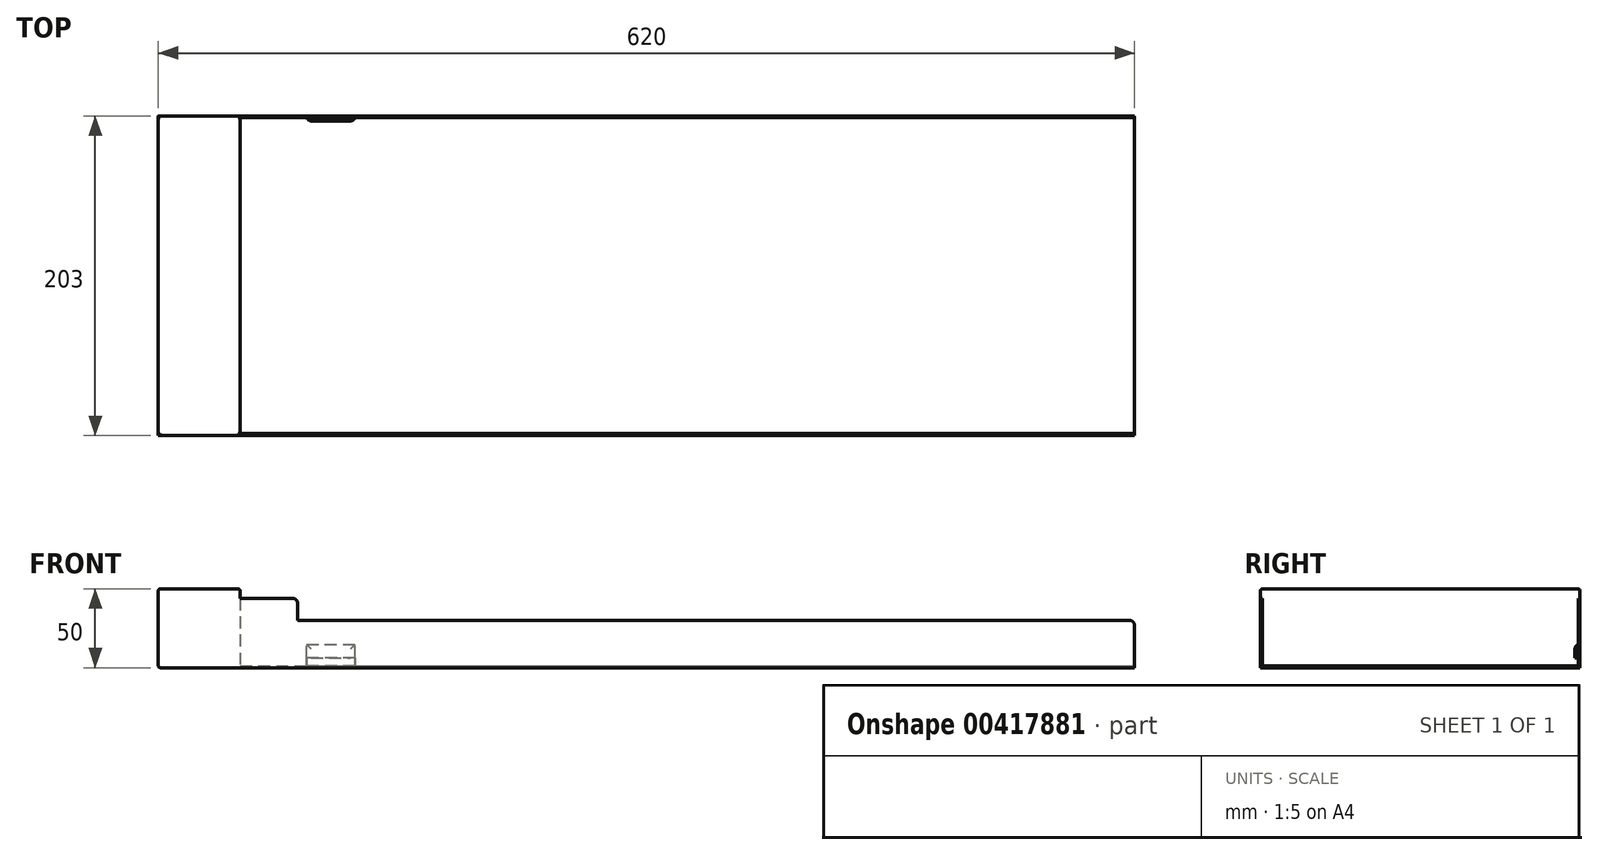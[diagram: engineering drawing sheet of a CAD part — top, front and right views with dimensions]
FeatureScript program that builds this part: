
annotation { "Feature Type Name" : "Feature", "Feature Type Description" : "" }
export const myFeature = defineFeature(function(context is Context, id is Id, definition is map)
    precondition{}
    {
        {
            var Q0;
            Q0=qCreatedBy(makeId("Top.planeOp"),FACE);
            var sketch = newSketch(context, id + "F0", { "sketchPlane" : qUnion([Q0])});
            skLineSegment(sketch, "E0.bottom", {"start": v(-97.62, 164.37) * mm, "end": v(522.38, 164.37) * mm});
            skLineSegment(sketch, "E0.top", {"start": v(-97.62, -38.63) * mm, "end": v(522.38, -38.63) * mm});
            skLineSegment(sketch, "E0.left", {"start": v(-97.62, 164.37) * mm, "end": v(-97.62, -38.63) * mm});
            skLineSegment(sketch, "E0.right", {"start": v(522.38, 164.37) * mm, "end": v(522.38, -38.63) * mm});
            skLineSegment(sketch, "E1.0", {"start": v(-45.62, 164.37) * mm, "end": v(-45.62, -38.63) * mm});
            skLineSegment(sketch, "E2.0", {"start": v(-97.62, 163.17) * mm, "end": v(522.38, 163.17) * mm});
            skLineSegment(sketch, "E3.0", {"start": v(-97.62, -37.43) * mm, "end": v(522.38, -37.43) * mm});
            skLineSegment(sketch, "E4", {"start": v(-9.17, -38.63) * mm, "end": v(-9.17, 164.37) * mm});
            skSolve(sketch);
        }
        {
            var Q0;
            {var subQ0=sQuery(id+"F0.wireOp",EDGE,"E0.left");Q0=makeQuery(id+"F0.imprint","IMPRINT",FACE,{"disambiguationData":[TD([[makeQuery(id+"F0.imprint","IMPRINT",EDGE,{"derivedFrom":subQ0}),1.0]])]});}
            extrude(context, id + "F1", {"entities" : qUnion([Q0]), "depth" : 50 * mm});
        }
        {
            var Q0;
            {var subQ0=sQuery(id+"F0.wireOp",EDGE,"E1.0");var subQ1=sQuery(id+"F0.wireOp",EDGE,"E0.top");var subQ2=makeQuery(id+"F0.imprint","INTERSECT",VERTEX,{"derivedFrom":[subQ1,subQ0]});Q0=makeQuery(id+"F0.imprint","IMPRINT",FACE,{"disambiguationData":[TD([[makeQuery(id+"F0.imprint","IMPRINT",EDGE,{"disambiguationData":[TD([[subQ2,-1.0]])],"derivedFrom":subQ1}),1.0]])]});}
            var Q1;
            {var subQ0=sQuery(id+"F0.wireOp",EDGE,"E1.0");var subQ1=sQuery(id+"F0.wireOp",EDGE,"E0.bottom");var subQ2=makeQuery(id+"F0.imprint","INTERSECT",VERTEX,{"derivedFrom":[subQ1,subQ0]});Q1=makeQuery(id+"F0.imprint","IMPRINT",FACE,{"disambiguationData":[TD([[makeQuery(id+"F0.imprint","IMPRINT",EDGE,{"disambiguationData":[TD([[subQ2,-1.0]])],"derivedFrom":subQ1}),-1.0]])]});}
            extrude(context, id + "F2", {"entities" : qUnion([Q0, Q1]), "operationType" : NewBodyOperationType.ADD, "depth" : 44 * mm});
        }
        {
            var Q0;
            {var subQ0=sQuery(id+"F0.wireOp",EDGE,"E0.right");var subQ1=sQuery(id+"F0.wireOp",EDGE,"E0.bottom");var subQ2=makeQuery(id+"F0.imprint","INTERSECT",VERTEX,{"derivedFrom":[subQ1,subQ0]});Q0=makeQuery(id+"F0.imprint","IMPRINT",FACE,{"disambiguationData":[TD([[makeQuery(id+"F0.imprint","IMPRINT",EDGE,{"disambiguationData":[TD([[subQ2,1.0]])],"derivedFrom":subQ1}),-1.0]])]});}
            var Q1;
            {var subQ0=sQuery(id+"F0.wireOp",EDGE,"E0.right");var subQ1=sQuery(id+"F0.wireOp",EDGE,"E0.top");var subQ2=makeQuery(id+"F0.imprint","INTERSECT",VERTEX,{"derivedFrom":[subQ1,subQ0]});Q1=makeQuery(id+"F0.imprint","IMPRINT",FACE,{"disambiguationData":[TD([[makeQuery(id+"F0.imprint","IMPRINT",EDGE,{"disambiguationData":[TD([[subQ2,1.0]])],"derivedFrom":subQ1}),1.0]])]});}
            extrude(context, id + "F3", {"entities" : qUnion([Q0, Q1]), "operationType" : NewBodyOperationType.ADD, "depth" : 30 * mm});
        }
        {
            var Q0;
            {var subQ0=sQuery(id+"F0.wireOp",EDGE,"E2.0");var subQ1=sQuery(id+"F0.wireOp",EDGE,"E0.right");var subQ2=makeQuery(id+"F0.imprint","INTERSECT",VERTEX,{"derivedFrom":[subQ1,subQ0]});Q0=makeQuery(id+"F0.imprint","IMPRINT",FACE,{"disambiguationData":[TD([[makeQuery(id+"F0.imprint","IMPRINT",EDGE,{"disambiguationData":[TD([[subQ2,-1.0]])],"derivedFrom":subQ1}),-1.0]])]});}
            var Q1;
            {var subQ0=sQuery(id+"F0.wireOp",EDGE,"E2.0");var subQ1=sQuery(id+"F0.wireOp",EDGE,"E1.0");var subQ2=makeQuery(id+"F0.imprint","INTERSECT",VERTEX,{"derivedFrom":[subQ1,subQ0]});Q1=makeQuery(id+"F0.imprint","IMPRINT",FACE,{"disambiguationData":[TD([[makeQuery(id+"F0.imprint","IMPRINT",EDGE,{"disambiguationData":[TD([[subQ2,-1.0]])],"derivedFrom":subQ1}),1.0]])]});}
            extrude(context, id + "F4", {"entities" : qUnion([Q0, Q1]), "operationType" : NewBodyOperationType.ADD, "depth" : 1.2 * mm});
        }
        {
            var Q0;
            Q0=makeQuery(id+"F1.opExtrude","CAP_EDGE",EDGE,{"disambiguationData":[OSD([sQuery(id+"F0.wireOp",EDGE,"E0.top")])],"isStart":false});
            var Q1;
            Q1=makeQuery(id+"F1.opExtrude","CAP_EDGE",EDGE,{"disambiguationData":[OSD([sQuery(id+"F0.wireOp",EDGE,"E0.bottom")])],"isStart":false});
            var Q2;
            Q2=makeQuery(id+"F1.opExtrude","CAP_EDGE",EDGE,{"disambiguationData":[OSD([sQuery(id+"F0.wireOp",EDGE,"E0.left")])],"isStart":false});
            var Q3;
            Q3=makeQuery(id+"F1.opExtrude","CAP_EDGE",EDGE,{"disambiguationData":[OSD([sQuery(id+"F0.wireOp",EDGE,"E0.left")])],"isStart":true});
            var Q4;
            Q4=makeQuery(id+"F1.opExtrude","CAP_EDGE",EDGE,{"disambiguationData":[OSD([sQuery(id+"F0.wireOp",EDGE,"E1.0")])],"isStart":false});
            var Q5;
            {var subQ0=sQuery(id+"F0.wireOp",EDGE,"E1.0");Q5=makeQuery(id+"F2.opExtrude","CAP_EDGE",EDGE,{"disambiguationData":[OSD([subQ0]),TDD([makeQuery(id+"F0.imprint","IMPRINT",EDGE,{"disambiguationData":[TD([[makeQuery(id+"F0.imprint","INTERSECT",VERTEX,{"derivedFrom":[sQuery(id+"F0.wireOp",EDGE,"E0.top"),subQ0]}),1.0]])],"derivedFrom":subQ0})])],"isStart":false});}
            fillet(context, id + "F5", {"entities" : qUnion([Q0, Q1, Q2, Q3, Q4, Q5]), "radius" : 1.2 * mm, "tangentPropagation" : true, "allowEdgeOverflow" : false});
        }
        {
            var Q0;
            {var subQ0=sQuery(id+"F0.wireOp",EDGE,"E4");Q0=makeQuery(id+"F2.opExtrude","CAP_EDGE",EDGE,{"disambiguationData":[OSD([subQ0]),TDD([makeQuery(id+"F0.imprint","IMPRINT",EDGE,{"disambiguationData":[TD([[makeQuery(id+"F0.imprint","INTERSECT",VERTEX,{"derivedFrom":[sQuery(id+"F0.wireOp",EDGE,"E0.top"),subQ0]}),-1.0]])],"derivedFrom":subQ0})])],"isStart":false});}
            var Q1;
            {var subQ0=sQuery(id+"F0.wireOp",EDGE,"E0.right");Q1=makeQuery(id+"F3.opExtrude","CAP_EDGE",EDGE,{"disambiguationData":[OSD([subQ0]),TDD([makeQuery(id+"F0.imprint","IMPRINT",EDGE,{"disambiguationData":[TD([[makeQuery(id+"F0.imprint","INTERSECT",VERTEX,{"derivedFrom":[sQuery(id+"F0.wireOp",EDGE,"E0.top"),subQ0]}),1.0]])],"derivedFrom":subQ0})])],"isStart":false});}
            var Q2;
            {var subQ0=sQuery(id+"F0.wireOp",EDGE,"E0.right");Q2=makeQuery(id+"F3.opExtrude","CAP_EDGE",EDGE,{"disambiguationData":[OSD([subQ0]),TDD([makeQuery(id+"F0.imprint","IMPRINT",EDGE,{"disambiguationData":[TD([[makeQuery(id+"F0.imprint","INTERSECT",VERTEX,{"derivedFrom":[sQuery(id+"F0.wireOp",EDGE,"E0.bottom"),subQ0]}),-1.0]])],"derivedFrom":subQ0})])],"isStart":false});}
            var Q3;
            {var subQ0=sQuery(id+"F0.wireOp",EDGE,"E4");Q3=makeQuery(id+"F2.opExtrude","CAP_EDGE",EDGE,{"disambiguationData":[OSD([subQ0]),TDD([makeQuery(id+"F0.imprint","IMPRINT",EDGE,{"disambiguationData":[TD([[makeQuery(id+"F0.imprint","INTERSECT",VERTEX,{"derivedFrom":[sQuery(id+"F0.wireOp",EDGE,"E0.bottom"),subQ0]}),1.0]])],"derivedFrom":subQ0})])],"isStart":false});}
            var Q4;
            {var subQ0=sQuery(id+"F0.wireOp",EDGE,"E4");Q4=makeQuery(id+"F3.opExtrude","CAP_EDGE",EDGE,{"disambiguationData":[OSD([subQ0]),TDD([makeQuery(id+"F0.imprint","IMPRINT",EDGE,{"disambiguationData":[TD([[makeQuery(id+"F0.imprint","INTERSECT",VERTEX,{"derivedFrom":[sQuery(id+"F0.wireOp",EDGE,"E0.bottom"),subQ0]}),1.0]])],"derivedFrom":subQ0})])],"isStart":false});}
            var Q5;
            {var subQ0=sQuery(id+"F0.wireOp",EDGE,"E4");Q5=makeQuery(id+"F3.opExtrude","CAP_EDGE",EDGE,{"disambiguationData":[OSD([subQ0]),TDD([makeQuery(id+"F0.imprint","IMPRINT",EDGE,{"disambiguationData":[TD([[makeQuery(id+"F0.imprint","INTERSECT",VERTEX,{"derivedFrom":[sQuery(id+"F0.wireOp",EDGE,"E0.top"),subQ0]}),-1.0]])],"derivedFrom":subQ0})])],"isStart":false});}
            var Q6;
            {var subQ0=sQuery(id+"F0.wireOp",EDGE,"E1.0");Q6=makeQuery(id+"F2.opExtrude","CAP_EDGE",EDGE,{"disambiguationData":[OSD([subQ0]),TDD([makeQuery(id+"F0.imprint","IMPRINT",EDGE,{"disambiguationData":[TD([[makeQuery(id+"F0.imprint","INTERSECT",VERTEX,{"derivedFrom":[sQuery(id+"F0.wireOp",EDGE,"E0.top"),subQ0]}),1.0]])],"derivedFrom":subQ0})])],"isStart":false});}
            fillet(context, id + "F6", {"entities" : qUnion([Q0, Q1, Q2, Q3, Q4, Q5, Q6]), "radius" : 3 * mm, "tangentPropagation" : true, "allowEdgeOverflow" : false});
        }
        {
            var Q0;
            {var subQ0=sQuery(id+"F0.wireOp",EDGE,"E2.0");Q0=makeQuery(id+"F3.boolean.opBoolean","MERGE",FACE,{"derivedFrom":[makeQuery(id+"F2.opExtrude","SWEPT_FACE",FACE,{"disambiguationData":[OSD([subQ0])]}),makeQuery(id+"F3.opExtrude","SWEPT_FACE",FACE,{"disambiguationData":[OSD([subQ0])]})]});}
            var sketch = newSketch(context, id + "F7", { "sketchPlane" : qUnion([Q0])});
            skLineSegment(sketch, "E5.bottom", {"start": v(-3.34, 1.18) * mm, "end": v(27.29, 1.18) * mm});
            skLineSegment(sketch, "E5.top", {"start": v(-3.34, 6.2) * mm, "end": v(27.29, 6.2) * mm});
            skLineSegment(sketch, "E5.left", {"start": v(-3.34, 1.18) * mm, "end": v(-3.34, 6.2) * mm});
            skLineSegment(sketch, "E5.right", {"start": v(27.29, 1.18) * mm, "end": v(27.29, 6.2) * mm});
            skSolve(sketch);
        }
        {
            var Q0;
            Q0 = qSketchRegion(id + "F7", true);
            extrude(context, id + "F8", {"entities" : qUnion([Q0]), "operationType" : NewBodyOperationType.REMOVE, "oppositeDirection" : true, "depth" : 25 * mm});
        }
        {
            var Q0;
            {var subQ0=sQuery(id+"F0.wireOp",EDGE,"E2.0");Q0=makeQuery(id+"F3.boolean.opBoolean","MERGE",FACE,{"derivedFrom":[makeQuery(id+"F2.opExtrude","SWEPT_FACE",FACE,{"disambiguationData":[OSD([subQ0])]}),makeQuery(id+"F3.opExtrude","SWEPT_FACE",FACE,{"disambiguationData":[OSD([subQ0])]})]});}
            var sketch = newSketch(context, id + "F9", { "sketchPlane" : qUnion([Q0])});
            skLineSegment(sketch, "E6.top", {"start": v(-3.34, 14.7) * mm, "end": v(27.29, 14.7) * mm});
            skLineSegment(sketch, "E6.left", {"start": v(-3.34, 6.2) * mm, "end": v(-3.34, 14.7) * mm});
            skLineSegment(sketch, "E6.right", {"start": v(27.29, 5.27) * mm, "end": v(27.29, 14.7) * mm});
            skSolve(sketch);
        }
        {
            var Q0;
            {var subQ0=sQuery(id+"F9.wireOp",EDGE,"E6.top");Q0=makeQuery(id+"F9.imprint","IMPRINT",FACE,{"disambiguationData":[TD([[makeQuery(id+"F9.imprint","IMPRINT",EDGE,{"derivedFrom":subQ0}),-1.0]])]});}
            extrude(context, id + "F10", {"entities" : qUnion([Q0]), "operationType" : NewBodyOperationType.ADD, "depth" : 2 * mm});
        }
        {
            var Q0;
            Q0=makeQuery(id+"F10.opExtrude","CAP_EDGE",EDGE,{"disambiguationData":[OSD([sQuery(id+"F9.wireOp",EDGE,"E6.top")])],"isStart":false});
            var Q1;
            Q1=makeQuery(id+"F10.opExtrude","CAP_EDGE",EDGE,{"disambiguationData":[OSD([sQuery(id+"F9.wireOp",EDGE,"E6.right")])],"isStart":false});
            var Q2;
            Q2=makeQuery(id+"F10.opExtrude","CAP_EDGE",EDGE,{"disambiguationData":[OSD([sQuery(id+"F9.wireOp",EDGE,"E6.left")])],"isStart":false});
            fillet(context, id + "F11", {"entities" : qUnion([Q0, Q1, Q2]), "radius" : 3 * mm, "tangentPropagation" : true, "allowEdgeOverflow" : false});
        }
    });
